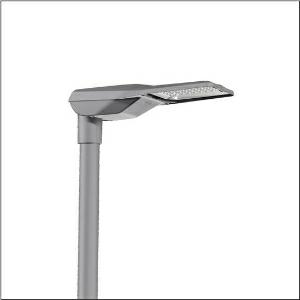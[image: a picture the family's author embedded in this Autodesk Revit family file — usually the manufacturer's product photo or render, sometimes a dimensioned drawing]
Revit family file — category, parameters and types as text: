
# Revit family: streetlight_sl_21_iq_mini___stw1_0a_5xe2e41g08hb_6f26
name_source: partatom
category: Lighting Fixtures
units: mm (PartAtom-declared; Revit-internal decimal feet)

## family parameters
Cut with Voids When Loaded = No
Host = Face
Light Source = No
Part Type = Normal
Room Calculation Point = No
Round Connector Dimension = Use Diameter
Shared = No

## types (1)
- --- (1 x LED, 9860 lm, 70.9 W, 4000K)
    Apparent Load = 71 VA
    CIE Flux Codes = 38 75 98 100 100
    Color Rendering = 70
    Color Temperature = 4000K
    Default Elevation = 1800 mm
    Description = Streetlight SL 21 mini, mast luminaire, primary light control with lens, of PMMA, primary optical cover: cover, of toughened safety glass, transparent, light distribution: STW1.0a, light emission: direct distribution, primary light characteristic: asymmetric, installation type: post-top, side-entry, LED, High Power LED, rated luminous flux: 9.860lm, luminous efficacy: 139lm/W, light colour: 740, colour temperature: 4000K, control gear: ECG iQ, control: Street-Remote, Auto-Match, Temp-Guard, Lumen-Switch, Night-Set, Smart-Wire, Light-Fading, Desk-Remote (wireless, voltage-free reading and setting of iQ features in the workshop via application-optimized NFC function/RFID function), optimised constant luminous flux control (CLO 2.0), mains connection: 220..240V, AC, 50/60Hz, start of lifetime: 71W, end of lifetime: 75W, reduction: 31W, luminaire housing, of diecast aluminium, powder-coated, Siteco® metallic grey (DB 702S), corrosivity category C5 according to DIN EN ISO 12944, length: 628mm, width: 235mm, height: 110mm, spigot size: 60/76mm (post-top) and 42/60/76mm (side-entry), mast flange for spigot size: 42mm: 5XC10008XM4, 60mm: 5XC10008XM2, 76/60mm: 5XC10108XM1, protection rating (complete): IP66, insulation class (complete): insulation class II (safety insulation), certification: CE, ENEC, VDE, impact resistance: IK09, permissible operating ambient temperature for outdoor applications: -40..+50°C, standard-compliant lighting for roads and squares, packaging unit: 1 piece

Light Distribution: STW1.0a
    Height = 110 mm
    Lamp = 1 x LED
    Lamp Light Flux = 9860 lm
    Lamp Power = 70.9 W
    Lamp count = 1
    Length = 625 mm
    Luminous efficacy = 139 lm/W
    Manufacturer = Siteco
    ModVariant = No
    Model = 5XE2E41G08HB
    Number of Poles = 1
    OnlyDefault = Yes
    Power Factor = 1
    Product Name = Streetlight SL 21 iQ mini | STW1.0a
    Product group = mast luminaire | pylon top
    ProductGroupID = 6100
    Protection Class = Protection class II
    Protection Degree = IP 66
    RLX_Detail_Level = 1
    RlxData = <blob elided: 92085 chars, md5=ce0b8837>
    Socket = socket
    Standby Power = 0 W
    System Light Flux = 9860 lm
    System Power = 71 W
    Type Comments = factory setting: luminous flux: 100 % | dim-lin: 254 | 711 mA
    Type Image = l_1003519.jpg
    URL = http://relux.com
    VarID = @adj_068999
    Voltage = 0 V
    Weight = 0.00 kg
    Width = 234 mm

## geometry (parser evidence)
native form markers: Blend x4, Sweep x12
no freeform markers — native parametric forms only
